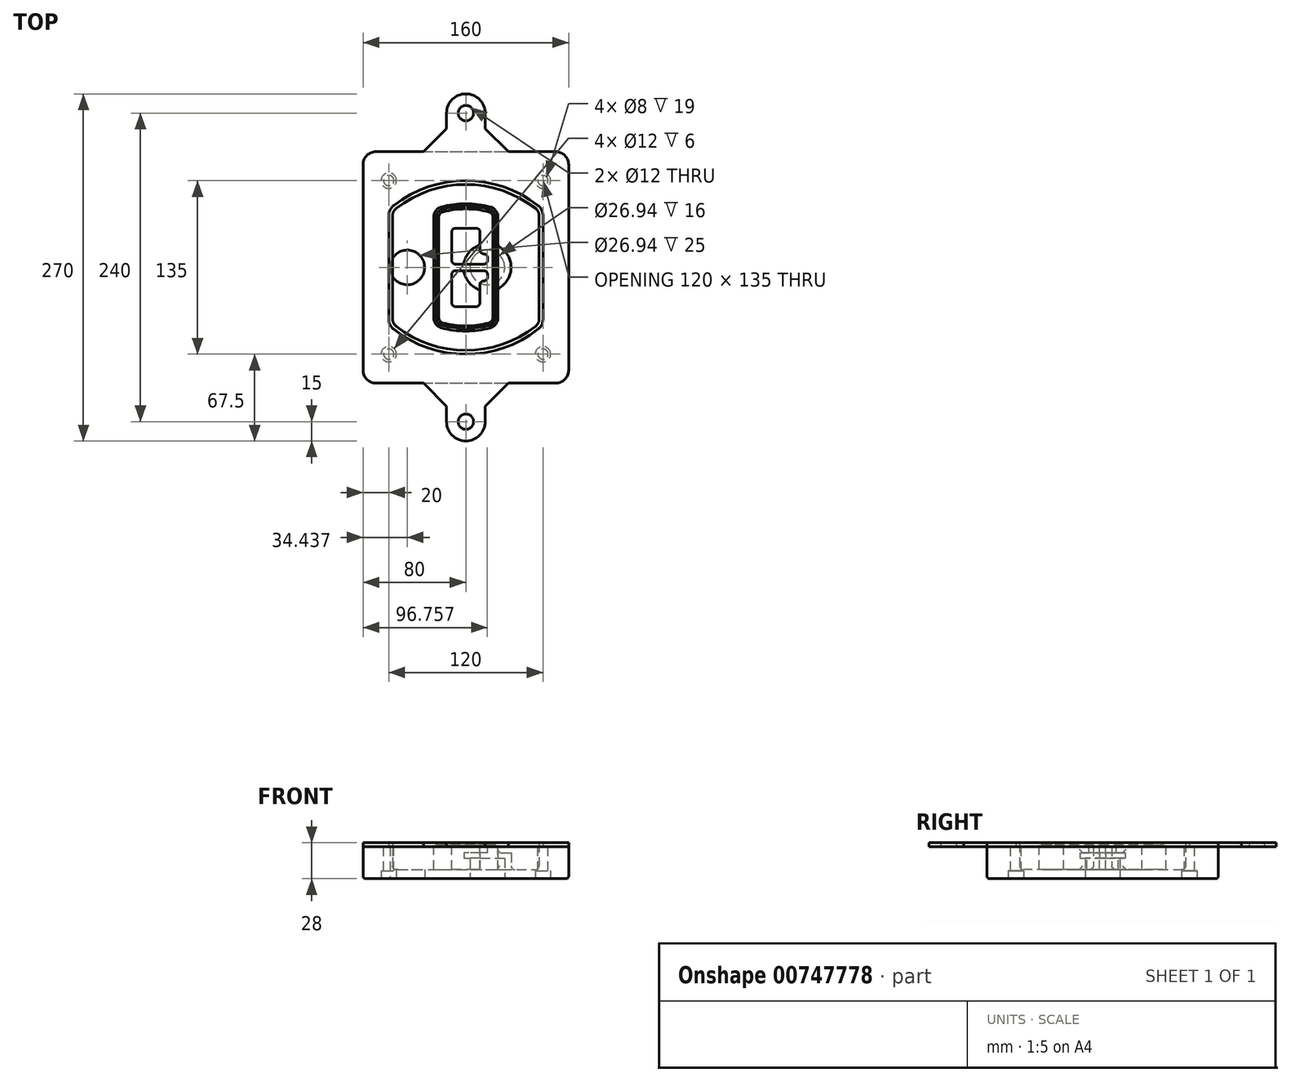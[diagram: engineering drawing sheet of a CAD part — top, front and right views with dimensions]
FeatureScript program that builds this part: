
annotation { "Feature Type Name" : "Feature", "Feature Type Description" : "" }
export const myFeature = defineFeature(function(context is Context, id is Id, definition is map)
    precondition{}
    {
        {
            var Q0;
            Q0=qCreatedBy(makeId("Top.planeOp"),FACE);
            var sketch = newSketch(context, id + "F0", { "sketchPlane" : qUnion([Q0])});
            skPoint(sketch, "E0.rect.middle", {"position": v(0, 0) * mm});
            skLineSegment(sketch, "E1.bottom", {"start": v(-70, -90) * mm, "end": v(70, -90) * mm});
            skLineSegment(sketch, "E1.top", {"start": v(-70, 90) * mm, "end": v(70, 90) * mm});
            skLineSegment(sketch, "E1.left", {"start": v(-80, -80) * mm, "end": v(-80, 80) * mm});
            skLineSegment(sketch, "E1.right", {"start": v(80, -80) * mm, "end": v(80, 80) * mm});
            skLineSegment(sketch, "E2", {"start": v(-80, 90) * mm, "end": v(80, -90) * mm, "construction": true});
            skLineSegment(sketch, "E3", {"start": v(80, 90) * mm, "end": v(-80, -90) * mm, "construction": true});
            skCircle(sketch, "E4", {"center": v(-60, 67.5) * mm, "radius": 4 * mm});
            skCircle(sketch, "E5", {"center": v(60, 67.5) * mm, "radius": 4 * mm});
            skCircle(sketch, "E6", {"center": v(60, -67.5) * mm, "radius": 4 * mm});
            skCircle(sketch, "E7", {"center": v(-60, -67.5) * mm, "radius": 4 * mm});
            skLineSegment(sketch, "E8", {"start": v(-60, 67.5) * mm, "end": v(60, 67.5) * mm, "construction": true});
            skLineSegment(sketch, "E9", {"start": v(60, 67.5) * mm, "end": v(60, -67.5) * mm, "construction": true});
            skLineSegment(sketch, "E10", {"start": v(60, -67.5) * mm, "end": v(-60, -67.5) * mm, "construction": true});
            skLineSegment(sketch, "E11", {"start": v(-60, -67.5) * mm, "end": v(-60, 67.5) * mm, "construction": true});
            skLineSegment(sketch, "E12", {"start": v(-60, 40.3) * mm, "end": v(-60, -40.3) * mm});
            skLineSegment(sketch, "E13", {"start": v(60, 40.3) * mm, "end": v(60, -40.3) * mm});
            skArc(sketch, "E14", {"start": v(56.15, 48.18) * mm, "mid": v(0, 67.5) * mm, "end": v(-56.15, 48.18) * mm});
            skArc(sketch, "E15", {"start": v(-56.15, -48.18) * mm, "mid": v(0, -67.5) * mm, "end": v(56.15, -48.18) * mm});
            skLineSegment(sketch, "E16", {"start": v(-60, 0) * mm, "end": v(60, 0) * mm, "construction": true});
            skPoint(sketch, "E17.visualSharp", {"position": v(-60, -45) * mm});
            skArc(sketch, "E17.filletArc", {"start": v(-60, -40.3) * mm, "mid": v(-58.99, -44.68) * mm, "end": v(-56.15, -48.18) * mm});
            skPoint(sketch, "E18.visualSharp", {"position": v(-60, 45) * mm});
            skArc(sketch, "E18.filletArc", {"start": v(-56.15, 48.18) * mm, "mid": v(-58.99, 44.68) * mm, "end": v(-60, 40.3) * mm});
            skPoint(sketch, "E19.visualSharp", {"position": v(60, 45) * mm});
            skArc(sketch, "E19.filletArc", {"start": v(60, 40.3) * mm, "mid": v(58.99, 44.68) * mm, "end": v(56.15, 48.18) * mm});
            skPoint(sketch, "E20.visualSharp", {"position": v(60, -45) * mm});
            skArc(sketch, "E20.filletArc", {"start": v(56.15, -48.18) * mm, "mid": v(58.99, -44.68) * mm, "end": v(60, -40.3) * mm});
            skPoint(sketch, "E21.visualSharp", {"position": v(-80, 90) * mm});
            skArc(sketch, "E21.filletArc", {"start": v(-70, 90) * mm, "mid": v(-77.07, 87.07) * mm, "end": v(-80, 80) * mm});
            skPoint(sketch, "E22.visualSharp", {"position": v(80, 90) * mm});
            skArc(sketch, "E22.filletArc", {"start": v(80, 80) * mm, "mid": v(77.07, 87.07) * mm, "end": v(70, 90) * mm});
            skPoint(sketch, "E23.visualSharp", {"position": v(80, -90) * mm});
            skArc(sketch, "E23.filletArc", {"start": v(70, -90) * mm, "mid": v(77.07, -87.07) * mm, "end": v(80, -80) * mm});
            skPoint(sketch, "E24.visualSharp", {"position": v(-80, -90) * mm});
            skArc(sketch, "E24.filletArc", {"start": v(-80, -80) * mm, "mid": v(-77.07, -87.07) * mm, "end": v(-70, -90) * mm});
            skArc(sketch, "E25.0", {"start": v(57, 40.3) * mm, "mid": v(56.3, 43.36) * mm, "end": v(54.3, 45.81) * mm});
            skLineSegment(sketch, "E25.1", {"start": v(57, 40.3) * mm, "end": v(57, -40.3) * mm});
            skArc(sketch, "E25.2", {"start": v(54.3, -45.81) * mm, "mid": v(56.3, -43.36) * mm, "end": v(57, -40.3) * mm});
            skArc(sketch, "E25.3", {"start": v(-54.3, -45.81) * mm, "mid": v(0, -64.5) * mm, "end": v(54.3, -45.81) * mm});
            skArc(sketch, "E25.4", {"start": v(-57, -40.3) * mm, "mid": v(-56.3, -43.36) * mm, "end": v(-54.3, -45.81) * mm});
            skArc(sketch, "E25.5", {"start": v(54.3, 45.81) * mm, "mid": v(0, 64.5) * mm, "end": v(-54.3, 45.81) * mm});
            skLineSegment(sketch, "E25.6", {"start": v(-57, 40.3) * mm, "end": v(-57, -40.3) * mm});
            skArc(sketch, "E25.7", {"start": v(-54.3, 45.81) * mm, "mid": v(-56.3, 43.36) * mm, "end": v(-57, 40.3) * mm});
            skArc(sketch, "E26.0", {"start": v(-58.62, 51.33) * mm, "mid": v(-62.58, 46.43) * mm, "end": v(-64, 40.3) * mm});
            skArc(sketch, "E26.1", {"start": v(58.62, 51.33) * mm, "mid": v(0, 71.5) * mm, "end": v(-58.62, 51.33) * mm});
            skArc(sketch, "E26.2", {"start": v(64, 40.3) * mm, "mid": v(62.58, 46.43) * mm, "end": v(58.62, 51.33) * mm});
            skLineSegment(sketch, "E26.3", {"start": v(64, 40.3) * mm, "end": v(64, -40.3) * mm});
            skArc(sketch, "E26.4", {"start": v(58.62, -51.33) * mm, "mid": v(62.58, -46.43) * mm, "end": v(64, -40.3) * mm});
            skLineSegment(sketch, "E26.5", {"start": v(-64, 40.3) * mm, "end": v(-64, -40.3) * mm});
            skArc(sketch, "E26.6", {"start": v(-58.62, -51.33) * mm, "mid": v(0, -71.5) * mm, "end": v(58.62, -51.33) * mm});
            skArc(sketch, "E26.7", {"start": v(-64, -40.3) * mm, "mid": v(-62.58, -46.43) * mm, "end": v(-58.62, -51.33) * mm});
            skSolve(sketch);
        }
        {
            var Q0;
            Q0=makeQuery(id+"F0.imprint","IMPRINT",FACE,{"disambiguationData":[TD([[makeQuery(id+"F0.imprint","IMPRINT",EDGE,{"derivedFrom":sQuery(id+"F0.wireOp",EDGE,"E1.bottom")}),1.0]])]});
            var Q1;
            Q1=makeQuery(id+"F0.imprint","IMPRINT",FACE,{"disambiguationData":[TD([[makeQuery(id+"F0.imprint","IMPRINT",EDGE,{"derivedFrom":sQuery(id+"F0.wireOp",EDGE,"E12")}),1.0]])]});
            var Q2;
            Q2=makeQuery(id+"F0.imprint","IMPRINT",FACE,{"disambiguationData":[TD([[makeQuery(id+"F0.imprint","IMPRINT",EDGE,{"derivedFrom":sQuery(id+"F0.wireOp",EDGE,"E25.0")}),1.0]])]});
            var Q3;
            Q3=makeQuery(id+"F0.imprint","IMPRINT",FACE,{"disambiguationData":[TD([[makeQuery(id+"F0.imprint","IMPRINT",EDGE,{"derivedFrom":sQuery(id+"F0.wireOp",EDGE,"E12")}),-1.0]])]});
            extrude(context, id + "F1", {"entities" : qUnion([Q0, Q1, Q2, Q3]), "oppositeDirection" : true, "depth" : 25 * mm, "offsetDistance" : 25 * mm});
        }
        {
            var Q0;
            Q0=makeQuery(id+"F0.imprint","IMPRINT",FACE,{"disambiguationData":[TD([[makeQuery(id+"F0.imprint","IMPRINT",EDGE,{"derivedFrom":sQuery(id+"F0.wireOp",EDGE,"E12")}),1.0]])]});
            var Q1;
            Q1 = qSketchRegion(id + "F4", true);
            extrude(context, id + "F2", {"entities" : qUnion([Q0, Q1]), "operationType" : NewBodyOperationType.ADD, "depth" : 3 * mm, "offsetDistance" : 25 * mm});
        }
        {
            var Q0;
            Q0=makeQuery(id+"F0.imprint","IMPRINT",FACE,{"disambiguationData":[TD([[makeQuery(id+"F0.imprint","IMPRINT",EDGE,{"derivedFrom":sQuery(id+"F0.wireOp",EDGE,"E25.0")}),1.0]])]});
            extrude(context, id + "F3", {"entities" : qUnion([Q0]), "operationType" : NewBodyOperationType.REMOVE, "oppositeDirection" : true, "depth" : 18 * mm});
        }
        {
            var Q0;
            Q0=makeQuery(id+"F2.opExtrude","CAP_FACE",FACE,{"disambiguationData":[OSD([sQuery(id+"F0.wireOp",EDGE,"E12"),sQuery(id+"F0.wireOp",EDGE,"E13"),sQuery(id+"F0.wireOp",EDGE,"E14"),sQuery(id+"F0.wireOp",EDGE,"E15"),sQuery(id+"F0.wireOp",EDGE,"E17.filletArc"),sQuery(id+"F0.wireOp",EDGE,"E18.filletArc"),sQuery(id+"F0.wireOp",EDGE,"E19.filletArc"),sQuery(id+"F0.wireOp",EDGE,"E20.filletArc"),sQuery(id+"F0.wireOp",EDGE,"E25.0"),sQuery(id+"F0.wireOp",EDGE,"E25.1"),sQuery(id+"F0.wireOp",EDGE,"E25.2"),sQuery(id+"F0.wireOp",EDGE,"E25.3"),sQuery(id+"F0.wireOp",EDGE,"E25.4"),sQuery(id+"F0.wireOp",EDGE,"E25.5"),sQuery(id+"F0.wireOp",EDGE,"E25.6"),sQuery(id+"F0.wireOp",EDGE,"E25.7")])],"isStart":false});
            var sketch = newSketch(context, id + "F4", { "sketchPlane" : qUnion([Q0])});
            skArc(sketch, "E27.0", {"start": v(-19.08, -46.97) * mm, "mid": v(0, -49.5) * mm, "end": v(19.08, -46.97) * mm});
            skArc(sketch, "E28.0", {"start": v(19.08, 46.97) * mm, "mid": v(0, 49.5) * mm, "end": v(-19.08, 46.97) * mm});
            skLineSegment(sketch, "E29", {"start": v(-25, 39.25) * mm, "end": v(-25, -39.25) * mm});
            skLineSegment(sketch, "E30", {"start": v(25, 39.25) * mm, "end": v(25, -39.25) * mm});
            skLineSegment(sketch, "E31", {"start": v(-25, 45.1) * mm, "end": v(25, 45.1) * mm, "construction": true});
            skLineSegment(sketch, "E32", {"start": v(-25, -45.1) * mm, "end": v(25, -45.1) * mm, "construction": true});
            skPoint(sketch, "E33.visualSharp", {"position": v(-25, 45.1) * mm});
            skArc(sketch, "E33.filletArc", {"start": v(-19.08, 46.97) * mm, "mid": v(-23.35, 44.11) * mm, "end": v(-25, 39.25) * mm});
            skPoint(sketch, "E34.visualSharp", {"position": v(25, 45.1) * mm});
            skArc(sketch, "E34.filletArc", {"start": v(25, 39.25) * mm, "mid": v(23.35, 44.11) * mm, "end": v(19.08, 46.97) * mm});
            skPoint(sketch, "E35.visualSharp", {"position": v(25, -45.1) * mm});
            skArc(sketch, "E35.filletArc", {"start": v(19.08, -46.97) * mm, "mid": v(23.35, -44.11) * mm, "end": v(25, -39.25) * mm});
            skPoint(sketch, "E36.visualSharp", {"position": v(-25, -45.1) * mm});
            skArc(sketch, "E36.filletArc", {"start": v(-25, -39.25) * mm, "mid": v(-23.35, -44.11) * mm, "end": v(-19.08, -46.97) * mm});
            skArc(sketch, "E37.0", {"start": v(54.3, 45.81) * mm, "mid": v(0, 64.5) * mm, "end": v(-54.3, 45.81) * mm});
            skArc(sketch, "E37.1", {"start": v(-54.3, 45.81) * mm, "mid": v(-56.3, 43.36) * mm, "end": v(-57, 40.3) * mm});
            skLineSegment(sketch, "E37.2", {"start": v(-57, 40.3) * mm, "end": v(-57, -40.3) * mm});
            skArc(sketch, "E37.3", {"start": v(-57, -40.3) * mm, "mid": v(-56.3, -43.36) * mm, "end": v(-54.3, -45.81) * mm});
            skArc(sketch, "E37.4", {"start": v(-54.3, -45.81) * mm, "mid": v(0, -64.5) * mm, "end": v(54.3, -45.81) * mm});
            skArc(sketch, "E37.5", {"start": v(54.3, -45.81) * mm, "mid": v(56.3, -43.36) * mm, "end": v(57, -40.3) * mm});
            skLineSegment(sketch, "E37.6", {"start": v(57, 40.3) * mm, "end": v(57, -40.3) * mm});
            skArc(sketch, "E37.7", {"start": v(57, 40.3) * mm, "mid": v(56.3, 43.36) * mm, "end": v(54.3, 45.81) * mm});
            skLineSegment(sketch, "E38.0", {"start": v(23, 39.25) * mm, "end": v(23, -39.25) * mm});
            skArc(sketch, "E38.1", {"start": v(18.56, -45.04) * mm, "mid": v(21.76, -42.9) * mm, "end": v(23, -39.25) * mm});
            skArc(sketch, "E38.2", {"start": v(-18.56, -45.04) * mm, "mid": v(0, -47.5) * mm, "end": v(18.56, -45.04) * mm});
            skArc(sketch, "E38.3", {"start": v(-23, -39.25) * mm, "mid": v(-21.76, -42.9) * mm, "end": v(-18.56, -45.04) * mm});
            skLineSegment(sketch, "E38.4", {"start": v(-23, 39.25) * mm, "end": v(-23, -39.25) * mm});
            skArc(sketch, "E38.5", {"start": v(23, 39.25) * mm, "mid": v(21.76, 42.9) * mm, "end": v(18.56, 45.04) * mm});
            skArc(sketch, "E38.6", {"start": v(-18.56, 45.04) * mm, "mid": v(-21.76, 42.9) * mm, "end": v(-23, 39.25) * mm});
            skArc(sketch, "E38.7", {"start": v(18.56, 45.04) * mm, "mid": v(0, 47.5) * mm, "end": v(-18.56, 45.04) * mm});
            skArc(sketch, "E39.0", {"start": v(21, 39.25) * mm, "mid": v(20.18, 41.68) * mm, "end": v(18.04, 43.1) * mm});
            skLineSegment(sketch, "E39.1", {"start": v(21, 39.25) * mm, "end": v(21, -39.25) * mm});
            skArc(sketch, "E39.2", {"start": v(18.04, -43.1) * mm, "mid": v(20.18, -41.68) * mm, "end": v(21, -39.25) * mm});
            skArc(sketch, "E39.3", {"start": v(-18.04, -43.1) * mm, "mid": v(0, -45.5) * mm, "end": v(18.04, -43.1) * mm});
            skArc(sketch, "E39.4", {"start": v(-21, -39.25) * mm, "mid": v(-20.18, -41.68) * mm, "end": v(-18.04, -43.1) * mm});
            skArc(sketch, "E39.5", {"start": v(18.04, 43.1) * mm, "mid": v(0, 45.5) * mm, "end": v(-18.04, 43.1) * mm});
            skLineSegment(sketch, "E39.6", {"start": v(-21, 39.25) * mm, "end": v(-21, -39.25) * mm});
            skArc(sketch, "E39.7", {"start": v(-18.04, 43.1) * mm, "mid": v(-20.18, 41.68) * mm, "end": v(-21, 39.25) * mm});
            skLineSegment(sketch, "E40", {"start": v(-25, 0) * mm, "end": v(25, 0) * mm, "construction": true});
            skLineSegment(sketch, "E41", {"start": v(-11, 5.5) * mm, "end": v(-11, 27.5) * mm});
            skLineSegment(sketch, "E42", {"start": v(-8, 30.5) * mm, "end": v(8, 30.5) * mm});
            skLineSegment(sketch, "E43", {"start": v(11, 27.5) * mm, "end": v(11, 13.5) * mm});
            skLineSegment(sketch, "E44", {"start": v(14, 10.5) * mm, "end": v(14, 10.5) * mm});
            skLineSegment(sketch, "E45", {"start": v(17, 7.5) * mm, "end": v(17, 5.5) * mm});
            skLineSegment(sketch, "E46", {"start": v(14, 2.5) * mm, "end": v(-8, 2.5) * mm});
            skPoint(sketch, "E47.visualSharp", {"position": v(-11, 30.5) * mm});
            skArc(sketch, "E47.filletArc", {"start": v(-8, 30.5) * mm, "mid": v(-10.12, 29.62) * mm, "end": v(-11, 27.5) * mm});
            skPoint(sketch, "E48.visualSharp", {"position": v(11, 30.5) * mm});
            skArc(sketch, "E48.filletArc", {"start": v(11, 27.5) * mm, "mid": v(10.12, 29.62) * mm, "end": v(8, 30.5) * mm});
            skPoint(sketch, "E49.visualSharp", {"position": v(11, 10.5) * mm});
            skArc(sketch, "E49.filletArc", {"start": v(11, 13.5) * mm, "mid": v(11.88, 11.38) * mm, "end": v(14, 10.5) * mm});
            skPoint(sketch, "E50.visualSharp", {"position": v(17, 10.5) * mm});
            skArc(sketch, "E50.filletArc", {"start": v(17, 7.5) * mm, "mid": v(16.12, 9.62) * mm, "end": v(14, 10.5) * mm});
            skPoint(sketch, "E51.visualSharp", {"position": v(17, 2.5) * mm});
            skArc(sketch, "E51.filletArc", {"start": v(14, 2.5) * mm, "mid": v(16.12, 3.38) * mm, "end": v(17, 5.5) * mm});
            skPoint(sketch, "E52.visualSharp", {"position": v(-11, 2.5) * mm});
            skArc(sketch, "E52.filletArc", {"start": v(-11, 5.5) * mm, "mid": v(-10.12, 3.38) * mm, "end": v(-8, 2.5) * mm});
            skLineSegment(sketch, "E53.0.MirrorCS", {"start": v(14, -2.5) * mm, "end": v(-8, -2.5) * mm});
            skArc(sketch, "E54.0.MirrorCS", {"start": v(-11, -5.5) * mm, "mid": v(-10.12, -3.38) * mm, "end": v(-8, -2.5) * mm});
            skLineSegment(sketch, "E55.0.MirrorCS", {"start": v(-11, -5.5) * mm, "end": v(-11, -27.5) * mm});
            skArc(sketch, "E56.0.MirrorCS", {"start": v(-8, -30.5) * mm, "mid": v(-10.12, -29.62) * mm, "end": v(-11, -27.5) * mm});
            skLineSegment(sketch, "E57.0.MirrorCS", {"start": v(-8, -30.5) * mm, "end": v(8, -30.5) * mm});
            skArc(sketch, "E58.0.MirrorCS", {"start": v(11, -27.5) * mm, "mid": v(10.12, -29.62) * mm, "end": v(8, -30.5) * mm});
            skLineSegment(sketch, "E59.0.MirrorCS", {"start": v(11, -27.5) * mm, "end": v(11, -13.5) * mm});
            skArc(sketch, "E60.0.MirrorCS", {"start": v(11, -13.5) * mm, "mid": v(11.88, -11.38) * mm, "end": v(14, -10.5) * mm});
            skArc(sketch, "E61.0.MirrorCS", {"start": v(17, -7.5) * mm, "mid": v(16.12, -9.62) * mm, "end": v(14, -10.5) * mm});
            skLineSegment(sketch, "E62.0.MirrorCS", {"start": v(17, -7.5) * mm, "end": v(17, -5.5) * mm});
            skArc(sketch, "E63.0.MirrorCS", {"start": v(14, -2.5) * mm, "mid": v(16.12, -3.38) * mm, "end": v(17, -5.5) * mm});
            skSolve(sketch);
        }
        {
            var Q0;
            Q0=makeQuery(id+"F4.imprint","IMPRINT",FACE,{"disambiguationData":[TD([[makeQuery(id+"F4.imprint","IMPRINT",EDGE,{"derivedFrom":sQuery(id+"F4.wireOp",EDGE,"E27.0")}),1.0]])]});
            var Q1;
            Q1=makeQuery(id+"F4.imprint","IMPRINT",FACE,{"disambiguationData":[TD([[makeQuery(id+"F4.imprint","IMPRINT",EDGE,{"derivedFrom":sQuery(id+"F4.wireOp",EDGE,"E38.0")}),-1.0]])]});
            var Q2;
            Q2=makeQuery(id+"F4.imprint","IMPRINT",FACE,{"disambiguationData":[TD([[makeQuery(id+"F4.imprint","IMPRINT",EDGE,{"derivedFrom":sQuery(id+"F4.wireOp",EDGE,"E39.0")}),1.0]])]});
            extrude(context, id + "F5", {"entities" : qUnion([Q0, Q1, Q2]), "operationType" : NewBodyOperationType.ADD, "endBound" : BoundingType.UP_TO_NEXT, "oppositeDirection" : true, "depth" : 25 * mm});
        }
        {
            var Q0;
            Q0=makeQuery(id+"F4.imprint","IMPRINT",FACE,{"disambiguationData":[TD([[makeQuery(id+"F4.imprint","IMPRINT",EDGE,{"derivedFrom":sQuery(id+"F4.wireOp",EDGE,"E38.0")}),-1.0]])]});
            extrude(context, id + "F6", {"entities" : qUnion([Q0]), "operationType" : NewBodyOperationType.REMOVE, "oppositeDirection" : true, "depth" : 2 * mm});
        }
        {
            var Q0;
            Q0=makeQuery(id+"F1.opExtrude","CAP_FACE",FACE,{"disambiguationData":[OSD([sQuery(id+"F0.wireOp",EDGE,"E1.bottom"),sQuery(id+"F0.wireOp",EDGE,"E1.top"),sQuery(id+"F0.wireOp",EDGE,"E1.left"),sQuery(id+"F0.wireOp",EDGE,"E1.right"),sQuery(id+"F0.wireOp",EDGE,"E4"),sQuery(id+"F0.wireOp",EDGE,"E5"),sQuery(id+"F0.wireOp",EDGE,"E6"),sQuery(id+"F0.wireOp",EDGE,"E7"),sQuery(id+"F0.wireOp",EDGE,"E21.filletArc"),sQuery(id+"F0.wireOp",EDGE,"E22.filletArc"),sQuery(id+"F0.wireOp",EDGE,"E23.filletArc"),sQuery(id+"F0.wireOp",EDGE,"E24.filletArc")])],"isStart":false});
            var sketch = newSketch(context, id + "F7", { "sketchPlane" : qUnion([Q0])});
            skCircle(sketch, "E64", {"center": v(16.76, 0) * mm, "radius": 13.47 * mm});
            skCircle(sketch, "E65", {"center": v(-45.56, 0) * mm, "radius": 13.47 * mm});
            skLineSegment(sketch, "E66", {"start": v(80, 0) * mm, "end": v(-80, 0) * mm});
            skCircle(sketch, "E67", {"center": v(16.76, 0) * mm, "radius": 18.47 * mm});
            skCircle(sketch, "E68", {"center": v(60, -67.5) * mm, "radius": 6 * mm});
            skCircle(sketch, "E69", {"center": v(-60, -67.5) * mm, "radius": 6 * mm});
            skCircle(sketch, "E70", {"center": v(-60, 67.5) * mm, "radius": 6 * mm});
            skCircle(sketch, "E71", {"center": v(60, 67.5) * mm, "radius": 6 * mm});
            skSolve(sketch);
        }
        {
            var Q0;
            {var subQ1=sQuery(id+"F7.wireOp",EDGE,"E66");var subQ4=sQuery(id+"F7.wireOp",EDGE,"E64");var subQ6=makeQuery(id+"F7.imprint","INTERSECT",VERTEX,{"disambiguationData":[OD(0.0)],"derivedFrom":[subQ4,subQ1]});Q0=makeQuery(id+"F7.imprint","IMPRINT",FACE,{"disambiguationData":[TD([[makeQuery(id+"F7.imprint","IMPRINT",EDGE,{"disambiguationData":[TD([[subQ6,-1.0]])],"derivedFrom":subQ4}),-1.0]])]});}
            var Q1;
            {var subQ0=sQuery(id+"F7.wireOp",EDGE,"E66");var subQ1=sQuery(id+"F7.wireOp",EDGE,"E64");var subQ3=makeQuery(id+"F7.imprint","INTERSECT",VERTEX,{"disambiguationData":[OD(0.0)],"derivedFrom":[subQ1,subQ0]});Q1=makeQuery(id+"F7.imprint","IMPRINT",FACE,{"disambiguationData":[TD([[makeQuery(id+"F7.imprint","IMPRINT",EDGE,{"disambiguationData":[TD([[subQ3,-1.0]])],"derivedFrom":subQ1}),1.0]])]});}
            var Q2;
            {var subQ0=sQuery(id+"F7.wireOp",EDGE,"E66");var subQ1=sQuery(id+"F7.wireOp",EDGE,"E64");var subQ3=makeQuery(id+"F7.imprint","INTERSECT",VERTEX,{"disambiguationData":[OD(0.0)],"derivedFrom":[subQ1,subQ0]});Q2=makeQuery(id+"F7.imprint","IMPRINT",FACE,{"disambiguationData":[TD([[makeQuery(id+"F7.imprint","IMPRINT",EDGE,{"disambiguationData":[TD([[subQ3,1.0]])],"derivedFrom":subQ1}),1.0]])]});}
            var Q3;
            {var subQ1=sQuery(id+"F7.wireOp",EDGE,"E66");var subQ4=sQuery(id+"F7.wireOp",EDGE,"E64");var subQ6=makeQuery(id+"F7.imprint","INTERSECT",VERTEX,{"disambiguationData":[OD(0.0)],"derivedFrom":[subQ4,subQ1]});Q3=makeQuery(id+"F7.imprint","IMPRINT",FACE,{"disambiguationData":[TD([[makeQuery(id+"F7.imprint","IMPRINT",EDGE,{"disambiguationData":[TD([[subQ6,1.0]])],"derivedFrom":subQ4}),-1.0]])]});}
            extrude(context, id + "F8", {"entities" : qUnion([Q0, Q1, Q2, Q3]), "operationType" : NewBodyOperationType.ADD, "oppositeDirection" : true, "depth" : 20 * mm});
        }
        {
            var Q0;
            {var subQ0=sQuery(id+"F7.wireOp",EDGE,"E66");var subQ1=sQuery(id+"F7.wireOp",EDGE,"E64");var subQ3=makeQuery(id+"F7.imprint","INTERSECT",VERTEX,{"disambiguationData":[OD(0.0)],"derivedFrom":[subQ1,subQ0]});Q0=makeQuery(id+"F7.imprint","IMPRINT",FACE,{"disambiguationData":[TD([[makeQuery(id+"F7.imprint","IMPRINT",EDGE,{"disambiguationData":[TD([[subQ3,-1.0]])],"derivedFrom":subQ1}),1.0]])]});}
            var Q1;
            {var subQ0=sQuery(id+"F7.wireOp",EDGE,"E66");var subQ1=sQuery(id+"F7.wireOp",EDGE,"E64");var subQ3=makeQuery(id+"F7.imprint","INTERSECT",VERTEX,{"disambiguationData":[OD(0.0)],"derivedFrom":[subQ1,subQ0]});Q1=makeQuery(id+"F7.imprint","IMPRINT",FACE,{"disambiguationData":[TD([[makeQuery(id+"F7.imprint","IMPRINT",EDGE,{"disambiguationData":[TD([[subQ3,1.0]])],"derivedFrom":subQ1}),1.0]])]});}
            extrude(context, id + "F9", {"entities" : qUnion([Q0, Q1]), "operationType" : NewBodyOperationType.REMOVE, "oppositeDirection" : true, "depth" : 16 * mm});
        }
        {
            var Q0;
            {var subQ0=sQuery(id+"F7.wireOp",EDGE,"E66");var subQ1=sQuery(id+"F7.wireOp",EDGE,"E65");var subQ3=makeQuery(id+"F7.imprint","INTERSECT",VERTEX,{"disambiguationData":[OD(0.0)],"derivedFrom":[subQ1,subQ0]});Q0=makeQuery(id+"F7.imprint","IMPRINT",FACE,{"disambiguationData":[TD([[makeQuery(id+"F7.imprint","IMPRINT",EDGE,{"disambiguationData":[TD([[subQ3,-1.0]])],"derivedFrom":subQ1}),1.0]])]});}
            var Q1;
            {var subQ0=sQuery(id+"F7.wireOp",EDGE,"E66");var subQ1=sQuery(id+"F7.wireOp",EDGE,"E65");var subQ3=makeQuery(id+"F7.imprint","INTERSECT",VERTEX,{"disambiguationData":[OD(0.0)],"derivedFrom":[subQ1,subQ0]});Q1=makeQuery(id+"F7.imprint","IMPRINT",FACE,{"disambiguationData":[TD([[makeQuery(id+"F7.imprint","IMPRINT",EDGE,{"disambiguationData":[TD([[subQ3,1.0]])],"derivedFrom":subQ1}),1.0]])]});}
            extrude(context, id + "F10", {"entities" : qUnion([Q0, Q1]), "operationType" : NewBodyOperationType.REMOVE, "oppositeDirection" : true, "depth" : 25 * mm});
        }
        {
            var Q0;
            Q0=makeQuery(id+"F7.imprint","IMPRINT",FACE,{"disambiguationData":[TD([[makeQuery(id+"F7.imprint","IMPRINT",EDGE,{"derivedFrom":sQuery(id+"F7.wireOp",EDGE,"E68")}),1.0]])]});
            var Q1;
            Q1=makeQuery(id+"F7.imprint","IMPRINT",FACE,{"disambiguationData":[TD([[makeQuery(id+"F7.imprint","IMPRINT",EDGE,{"derivedFrom":makeQuery(id+"F1.opExtrude","CAP_EDGE",EDGE,{"disambiguationData":[OSD([sQuery(id+"F0.wireOp",EDGE,"E5")])],"isStart":false})}),-1.0]])]});
            var Q2;
            Q2=makeQuery(id+"F7.imprint","IMPRINT",FACE,{"disambiguationData":[TD([[makeQuery(id+"F7.imprint","IMPRINT",EDGE,{"derivedFrom":sQuery(id+"F7.wireOp",EDGE,"E69")}),1.0]])]});
            var Q3;
            Q3=makeQuery(id+"F7.imprint","IMPRINT",FACE,{"disambiguationData":[TD([[makeQuery(id+"F7.imprint","IMPRINT",EDGE,{"derivedFrom":makeQuery(id+"F1.opExtrude","CAP_EDGE",EDGE,{"disambiguationData":[OSD([sQuery(id+"F0.wireOp",EDGE,"E4")])],"isStart":false})}),-1.0]])]});
            var Q4;
            Q4=makeQuery(id+"F7.imprint","IMPRINT",FACE,{"disambiguationData":[TD([[makeQuery(id+"F7.imprint","IMPRINT",EDGE,{"derivedFrom":sQuery(id+"F7.wireOp",EDGE,"E70")}),1.0]])]});
            var Q5;
            Q5=makeQuery(id+"F7.imprint","IMPRINT",FACE,{"disambiguationData":[TD([[makeQuery(id+"F7.imprint","IMPRINT",EDGE,{"derivedFrom":makeQuery(id+"F1.opExtrude","CAP_EDGE",EDGE,{"disambiguationData":[OSD([sQuery(id+"F0.wireOp",EDGE,"E7")])],"isStart":false})}),-1.0]])]});
            var Q6;
            Q6=makeQuery(id+"F7.imprint","IMPRINT",FACE,{"disambiguationData":[TD([[makeQuery(id+"F7.imprint","IMPRINT",EDGE,{"derivedFrom":sQuery(id+"F7.wireOp",EDGE,"E71")}),1.0]])]});
            var Q7;
            Q7=makeQuery(id+"F7.imprint","IMPRINT",FACE,{"disambiguationData":[TD([[makeQuery(id+"F7.imprint","IMPRINT",EDGE,{"derivedFrom":makeQuery(id+"F1.opExtrude","CAP_EDGE",EDGE,{"disambiguationData":[OSD([sQuery(id+"F0.wireOp",EDGE,"E6")])],"isStart":false})}),-1.0]])]});
            extrude(context, id + "F11", {"entities" : qUnion([Q0, Q1, Q2, Q3, Q4, Q5, Q6, Q7]), "operationType" : NewBodyOperationType.REMOVE, "oppositeDirection" : true, "depth" : 6 * mm});
        }
        {
            var Q0;
            Q0=makeQuery(id+"F9.boolean.opBoolean","COPY",FACE,{"derivedFrom":makeQuery(id+"F9.opExtrude","CAP_FACE",FACE,{"disambiguationData":[OSD([sQuery(id+"F7.wireOp",EDGE,"E64")])],"isStart":false})});
            var sketch = newSketch(context, id + "F12", { "sketchPlane" : qUnion([Q0])});
            skArc(sketch, "E72.0", {"start": v(11, 17.55) * mm, "mid": v(2.57, 11.82) * mm, "end": v(-1.54, 2.5) * mm});
            skArc(sketch, "E72.1", {"start": v(-1.54, -2.5) * mm, "mid": v(2.57, -11.82) * mm, "end": v(11, -17.55) * mm});
            skLineSegment(sketch, "E73", {"start": v(-1.54, -2.5) * mm, "end": v(14, -2.5) * mm});
            skLineSegment(sketch, "E74.0", {"start": v(14, 2.5) * mm, "end": v(-1.54, 2.5) * mm});
            skArc(sketch, "E74.1", {"start": v(14, 2.5) * mm, "mid": v(16.12, 3.38) * mm, "end": v(17, 5.5) * mm});
            skLineSegment(sketch, "E74.2", {"start": v(17, 7.5) * mm, "end": v(17, 5.5) * mm});
            skArc(sketch, "E74.3", {"start": v(17, 7.5) * mm, "mid": v(16.12, 9.62) * mm, "end": v(14, 10.5) * mm});
            skArc(sketch, "E74.4", {"start": v(11, 13.5) * mm, "mid": v(11.88, 11.38) * mm, "end": v(14, 10.5) * mm});
            skLineSegment(sketch, "E74.5", {"start": v(11, 17.55) * mm, "end": v(11, 13.5) * mm});
            skLineSegment(sketch, "E74.7", {"start": v(14, -2.5) * mm, "end": v(-1.54, -2.5) * mm});
            skArc(sketch, "E74.8", {"start": v(14, -2.5) * mm, "mid": v(16.12, -3.38) * mm, "end": v(17, -5.5) * mm});
            skLineSegment(sketch, "E74.9", {"start": v(17, -7.5) * mm, "end": v(17, -5.5) * mm});
            skArc(sketch, "E74.10", {"start": v(17, -7.5) * mm, "mid": v(16.12, -9.62) * mm, "end": v(14, -10.5) * mm});
            skArc(sketch, "E74.11", {"start": v(11, -13.5) * mm, "mid": v(11.88, -11.38) * mm, "end": v(14, -10.5) * mm});
            skLineSegment(sketch, "E74.12", {"start": v(11, -17.55) * mm, "end": v(11, -13.5) * mm});
            skPoint(sketch, "E75.orphan", {"position": v(11, -27.5) * mm});
            skPoint(sketch, "E76.orphan", {"position": v(-8, -2.5) * mm});
            skPoint(sketch, "E77.orphan", {"position": v(-8, 2.5) * mm});
            skPoint(sketch, "E78.orphan", {"position": v(11, 27.5) * mm});
            skSolve(sketch);
        }
        {
            var Q0;
            {var subQ7=sQuery(id+"F12.wireOp",EDGE,"E72.0");var subQ14=sQuery(id+"F12.wireOp",EDGE,"E72.1");var subQ16=sQuery(id+"F12.wireOp",EDGE,"E74.1");var subQ18=sQuery(id+"F12.wireOp",EDGE,"E74.8");Q0=qUnion([makeQuery(id+"F12.imprint","IMPRINT",FACE,{"disambiguationData":[TD([[makeQuery(id+"F12.imprint","IMPRINT",EDGE,{"derivedFrom":subQ7}),1.0]])]}),makeQuery(id+"F12.imprint","IMPRINT",FACE,{"disambiguationData":[TD([[makeQuery(id+"F12.imprint","IMPRINT",EDGE,{"derivedFrom":subQ14}),1.0]])]}),makeQuery(id+"F12.imprint","IMPRINT",FACE,{"disambiguationData":[TD([[makeQuery(id+"F12.imprint","IMPRINT",EDGE,{"derivedFrom":subQ16}),1.0]])]}),makeQuery(id+"F12.imprint","IMPRINT",FACE,{"disambiguationData":[TD([[makeQuery(id+"F12.imprint","IMPRINT",EDGE,{"derivedFrom":subQ18}),-1.0]])]})]);}
            var Q1;
            Q1=makeQuery(id+"F5.boolean.opBoolean","SPLIT",FACE,{"disambiguationData":[TD([makeQuery(id+"F5.opExtrude","SWEPT_FACE",FACE,{"disambiguationData":[OSD([sQuery(id+"F4.wireOp",EDGE,"E41")])]})])],"derivedFrom":makeQuery(id+"F3.boolean.opBoolean","COPY",FACE,{"derivedFrom":makeQuery(id+"F3.opExtrude","CAP_FACE",FACE,{"disambiguationData":[OSD([sQuery(id+"F0.wireOp",EDGE,"E25.0"),sQuery(id+"F0.wireOp",EDGE,"E25.1"),sQuery(id+"F0.wireOp",EDGE,"E25.2"),sQuery(id+"F0.wireOp",EDGE,"E25.3"),sQuery(id+"F0.wireOp",EDGE,"E25.4"),sQuery(id+"F0.wireOp",EDGE,"E25.5"),sQuery(id+"F0.wireOp",EDGE,"E25.6"),sQuery(id+"F0.wireOp",EDGE,"E25.7")])],"isStart":false})})});
            extrude(context, id + "F13", {"entities" : qUnion([Q0]), "operationType" : NewBodyOperationType.REMOVE, "endBound" : BoundingType.UP_TO_SURFACE, "endBoundEntityFace" : qUnion([Q1]), "depth" : 25 * mm});
        }
        {
            var Q0;
            Q0=makeQuery(id+"F3.boolean.opBoolean","COPY",EDGE,{"derivedFrom":makeQuery(id+"F3.opExtrude","CAP_EDGE",EDGE,{"disambiguationData":[OSD([sQuery(id+"F0.wireOp",EDGE,"E25.6")])],"isStart":false})});
            var Q1;
            Q1=makeQuery(id+"F8.boolean.opBoolean","INTERSECT",EDGE,{"derivedFrom":[makeQuery(id+"F5.opExtrude","SWEPT_FACE",FACE,{"disambiguationData":[OSD([sQuery(id+"F4.wireOp",EDGE,"E30")])]}),makeQuery(id+"F8.opExtrude","CAP_FACE",FACE,{"disambiguationData":[OSD([sQuery(id+"F7.wireOp",EDGE,"E67")])],"isStart":false})]});
            var Q2;
            Q2=makeQuery(id+"F8.boolean.opBoolean","INTERSECT",EDGE,{"disambiguationData":[OD(1.0)],"derivedFrom":[makeQuery(id+"F5.opExtrude","SWEPT_FACE",FACE,{"disambiguationData":[OSD([sQuery(id+"F4.wireOp",EDGE,"E30")])]}),makeQuery(id+"F8.opExtrude","SWEPT_FACE",FACE,{"disambiguationData":[OSD([sQuery(id+"F7.wireOp",EDGE,"E67")])]})]});
            var Q3;
            {var subQ0=makeQuery(id+"F3.boolean.opBoolean","COPY",FACE,{"derivedFrom":makeQuery(id+"F3.opExtrude","CAP_FACE",FACE,{"disambiguationData":[OSD([sQuery(id+"F0.wireOp",EDGE,"E25.0"),sQuery(id+"F0.wireOp",EDGE,"E25.1"),sQuery(id+"F0.wireOp",EDGE,"E25.2"),sQuery(id+"F0.wireOp",EDGE,"E25.3"),sQuery(id+"F0.wireOp",EDGE,"E25.4"),sQuery(id+"F0.wireOp",EDGE,"E25.5"),sQuery(id+"F0.wireOp",EDGE,"E25.6"),sQuery(id+"F0.wireOp",EDGE,"E25.7")])],"isStart":false})});var subQ1=sQuery(id+"F4.wireOp",EDGE,"E30");Q3=makeQuery(id+"F8.boolean.opBoolean","SPLIT",EDGE,{"disambiguationData":[TD([makeQuery(id+"F5.opExtrude","SWEPT_FACE",FACE,{"disambiguationData":[OSD([sQuery(id+"F4.wireOp",EDGE,"E35.filletArc")])]})])],"derivedFrom":makeQuery(id+"F5.opExtrude","TWEAK_EDGE",EDGE,{"derivedFrom":[subQ0,makeQuery(id+"F4.imprint","IMPRINT",EDGE,{"derivedFrom":subQ1})]})});}
            var Q4;
            {var subQ0=sQuery(id+"F0.wireOp",EDGE,"E25.0");var subQ1=sQuery(id+"F0.wireOp",EDGE,"E25.1");var subQ2=sQuery(id+"F0.wireOp",EDGE,"E25.2");var subQ3=sQuery(id+"F0.wireOp",EDGE,"E25.3");var subQ4=sQuery(id+"F0.wireOp",EDGE,"E25.4");var subQ5=sQuery(id+"F0.wireOp",EDGE,"E25.5");var subQ6=sQuery(id+"F0.wireOp",EDGE,"E25.6");var subQ7=sQuery(id+"F0.wireOp",EDGE,"E25.7");Q4=makeQuery(id+"F8.boolean.opBoolean","INTERSECT",EDGE,{"derivedFrom":[makeQuery(id+"F5.boolean.opBoolean","SPLIT",FACE,{"disambiguationData":[TD([makeQuery(id+"F2.opExtrude","SWEPT_FACE",FACE,{"disambiguationData":[OSD([subQ0])]})])],"derivedFrom":makeQuery(id+"F3.boolean.opBoolean","COPY",FACE,{"derivedFrom":makeQuery(id+"F3.opExtrude","CAP_FACE",FACE,{"disambiguationData":[OSD([subQ0,subQ1,subQ2,subQ3,subQ4,subQ5,subQ6,subQ7])],"isStart":false})})}),makeQuery(id+"F8.opExtrude","SWEPT_FACE",FACE,{"disambiguationData":[OSD([sQuery(id+"F7.wireOp",EDGE,"E67")])]})]});}
            var Q5;
            Q5=makeQuery(id+"F8.boolean.opBoolean","INTERSECT",EDGE,{"disambiguationData":[OD(0.0)],"derivedFrom":[makeQuery(id+"F5.opExtrude","SWEPT_FACE",FACE,{"disambiguationData":[OSD([sQuery(id+"F4.wireOp",EDGE,"E30")])]}),makeQuery(id+"F8.opExtrude","SWEPT_FACE",FACE,{"disambiguationData":[OSD([sQuery(id+"F7.wireOp",EDGE,"E67")])]})]});
            fillet(context, id + "F14", {"entities" : qUnion([Q0, Q1, Q2, Q3, Q4, Q5]), "radius" : 3 * mm, "tangentPropagation" : true, "allowEdgeOverflow" : false});
        }
        {
            var Q0;
            Q0=qCreatedBy(makeId("Top.planeOp"),FACE);
            var sketch = newSketch(context, id + "F15", { "sketchPlane" : qUnion([Q0])});
            skLineSegment(sketch, "E79.0", {"start": v(-70, 90) * mm, "end": v(70, 90) * mm});
            skArc(sketch, "E80.0", {"start": v(-70, 90) * mm, "mid": v(-77.07, 87.07) * mm, "end": v(-80, 80) * mm});
            skLineSegment(sketch, "E80.1", {"start": v(-80, -80) * mm, "end": v(-80, 80) * mm});
            skArc(sketch, "E80.2", {"start": v(-80, -80) * mm, "mid": v(-77.07, -87.07) * mm, "end": v(-70, -90) * mm});
            skLineSegment(sketch, "E81.0", {"start": v(-70, -90) * mm, "end": v(70, -90) * mm});
            skArc(sketch, "E81.1", {"start": v(70, -90) * mm, "mid": v(77.07, -87.07) * mm, "end": v(80, -80) * mm});
            skLineSegment(sketch, "E81.2", {"start": v(80, -80) * mm, "end": v(80, 80) * mm});
            skArc(sketch, "E82.0", {"start": v(80, 80) * mm, "mid": v(77.07, 87.07) * mm, "end": v(70, 90) * mm});
            skArc(sketch, "E82.1", {"start": v(56.15, 48.18) * mm, "mid": v(0, 67.5) * mm, "end": v(-56.15, 48.18) * mm});
            skArc(sketch, "E82.2", {"start": v(60, 40.3) * mm, "mid": v(58.99, 44.68) * mm, "end": v(56.15, 48.18) * mm});
            skLineSegment(sketch, "E82.3", {"start": v(60, 40.3) * mm, "end": v(60, -40.3) * mm});
            skArc(sketch, "E82.4", {"start": v(-56.15, -48.18) * mm, "mid": v(0, -67.5) * mm, "end": v(56.15, -48.18) * mm});
            skArc(sketch, "E82.5", {"start": v(56.15, -48.18) * mm, "mid": v(58.99, -44.68) * mm, "end": v(60, -40.3) * mm});
            skArc(sketch, "E83.0", {"start": v(-56.15, 48.18) * mm, "mid": v(-58.99, 44.68) * mm, "end": v(-60, 40.3) * mm});
            skLineSegment(sketch, "E83.1", {"start": v(-60, 40.3) * mm, "end": v(-60, -40.3) * mm});
            skArc(sketch, "E83.2", {"start": v(-60, -40.3) * mm, "mid": v(-58.99, -44.68) * mm, "end": v(-56.15, -48.18) * mm});
            skLineSegment(sketch, "E84", {"start": v(0, 90) * mm, "end": v(0, 120) * mm, "construction": true});
            skLineSegment(sketch, "E85", {"start": v(15, 120) * mm, "end": v(15, 108) * mm});
            skLineSegment(sketch, "E86", {"start": v(15, 108) * mm, "end": v(33, 90) * mm});
            skLineSegment(sketch, "E87", {"start": v(-15, 120) * mm, "end": v(-15, 108) * mm});
            skLineSegment(sketch, "E88", {"start": v(-15, 108) * mm, "end": v(-33, 90) * mm});
            skArc(sketch, "E89", {"start": v(15, 120) * mm, "mid": v(0, 135) * mm, "end": v(-15, 120) * mm});
            skCircle(sketch, "E90", {"center": v(0, 120) * mm, "radius": 6 * mm});
            skArc(sketch, "E91.MirrorCS", {"start": v(-15, 120) * mm, "mid": v(0, 135) * mm, "end": v(15, 120) * mm});
            skLineSegment(sketch, "E92", {"start": v(-80, 0) * mm, "end": v(80, 0) * mm, "construction": true});
            skLineSegment(sketch, "E93.MirrorCS", {"start": v(-15, -120) * mm, "end": v(-15, -108) * mm});
            skLineSegment(sketch, "E94.MirrorCS", {"start": v(15, -108) * mm, "end": v(33, -90) * mm});
            skCircle(sketch, "E95.MirrorC", {"center": v(0, -120) * mm, "radius": 6 * mm});
            skLineSegment(sketch, "E96.MirrorCS", {"start": v(-15, -108) * mm, "end": v(-33, -90) * mm});
            skArc(sketch, "E97.MirrorCS", {"start": v(15, -120) * mm, "mid": v(0, -135) * mm, "end": v(-15, -120) * mm});
            skLineSegment(sketch, "E98.MirrorCS", {"start": v(15, -120) * mm, "end": v(15, -108) * mm});
            skArc(sketch, "E99.MirrorCS", {"start": v(-15, -120) * mm, "mid": v(0, -135) * mm, "end": v(15, -120) * mm});
            skLineSegment(sketch, "E100.MirrorCS", {"start": v(0, -90) * mm, "end": v(0, -120) * mm, "construction": true});
            skArc(sketch, "E101.MirrorCS", {"start": v(56.15, -48.18) * mm, "mid": v(0, -67.5) * mm, "end": v(-56.15, -48.18) * mm});
            skSolve(sketch);
        }
        {
            var Q0;
            Q0=makeQuery(id+"F1.opExtrude","CAP_EDGE",EDGE,{"disambiguationData":[OSD([sQuery(id+"F0.wireOp",EDGE,"E1.bottom")])],"isStart":false});
            fillet(context, id + "F16", {"entities" : qUnion([Q0]), "radius" : 2 * mm, "tangentPropagation" : true, "allowEdgeOverflow" : false});
        }
        {
            var Q0;
            Q0=makeQuery(id+"F15.imprint","IMPRINT",FACE,{"disambiguationData":[TD([[makeQuery(id+"F15.imprint","IMPRINT",EDGE,{"derivedFrom":sQuery(id+"F15.wireOp",EDGE,"E87")}),1.0]])]});
            var Q1;
            Q1=makeQuery(id+"F15.imprint","IMPRINT",FACE,{"disambiguationData":[TD([[makeQuery(id+"F15.imprint","IMPRINT",EDGE,{"derivedFrom":sQuery(id+"F15.wireOp",EDGE,"E93.MirrorCS")}),-1.0]])]});
            var Q2;
            {var subQ5=sQuery(id+"F15.wireOp",EDGE,"E80.0");Q2=makeQuery(id+"F15.imprint","IMPRINT",FACE,{"disambiguationData":[TD([[makeQuery(id+"F15.imprint","IMPRINT",EDGE,{"derivedFrom":subQ5}),1.0]])]});}
            var Q3;
            Q3=makeQuery(id+"F2.opExtrude","CAP_FACE",FACE,{"disambiguationData":[OSD([sQuery(id+"F0.wireOp",EDGE,"E12"),sQuery(id+"F0.wireOp",EDGE,"E13"),sQuery(id+"F0.wireOp",EDGE,"E14"),sQuery(id+"F0.wireOp",EDGE,"E15"),sQuery(id+"F0.wireOp",EDGE,"E17.filletArc"),sQuery(id+"F0.wireOp",EDGE,"E18.filletArc"),sQuery(id+"F0.wireOp",EDGE,"E19.filletArc"),sQuery(id+"F0.wireOp",EDGE,"E20.filletArc"),sQuery(id+"F0.wireOp",EDGE,"E25.0"),sQuery(id+"F0.wireOp",EDGE,"E25.1"),sQuery(id+"F0.wireOp",EDGE,"E25.2"),sQuery(id+"F0.wireOp",EDGE,"E25.3"),sQuery(id+"F0.wireOp",EDGE,"E25.4"),sQuery(id+"F0.wireOp",EDGE,"E25.5"),sQuery(id+"F0.wireOp",EDGE,"E25.6"),sQuery(id+"F0.wireOp",EDGE,"E25.7")])],"isStart":false});
            extrude(context, id + "F17", {"entities" : qUnion([Q0, Q1, Q2]), "endBound" : BoundingType.UP_TO_SURFACE, "depth" : 25 * mm, "endBoundEntityFace" : qUnion([Q3]), "offsetDistance" : 25 * mm});
        }
    });
